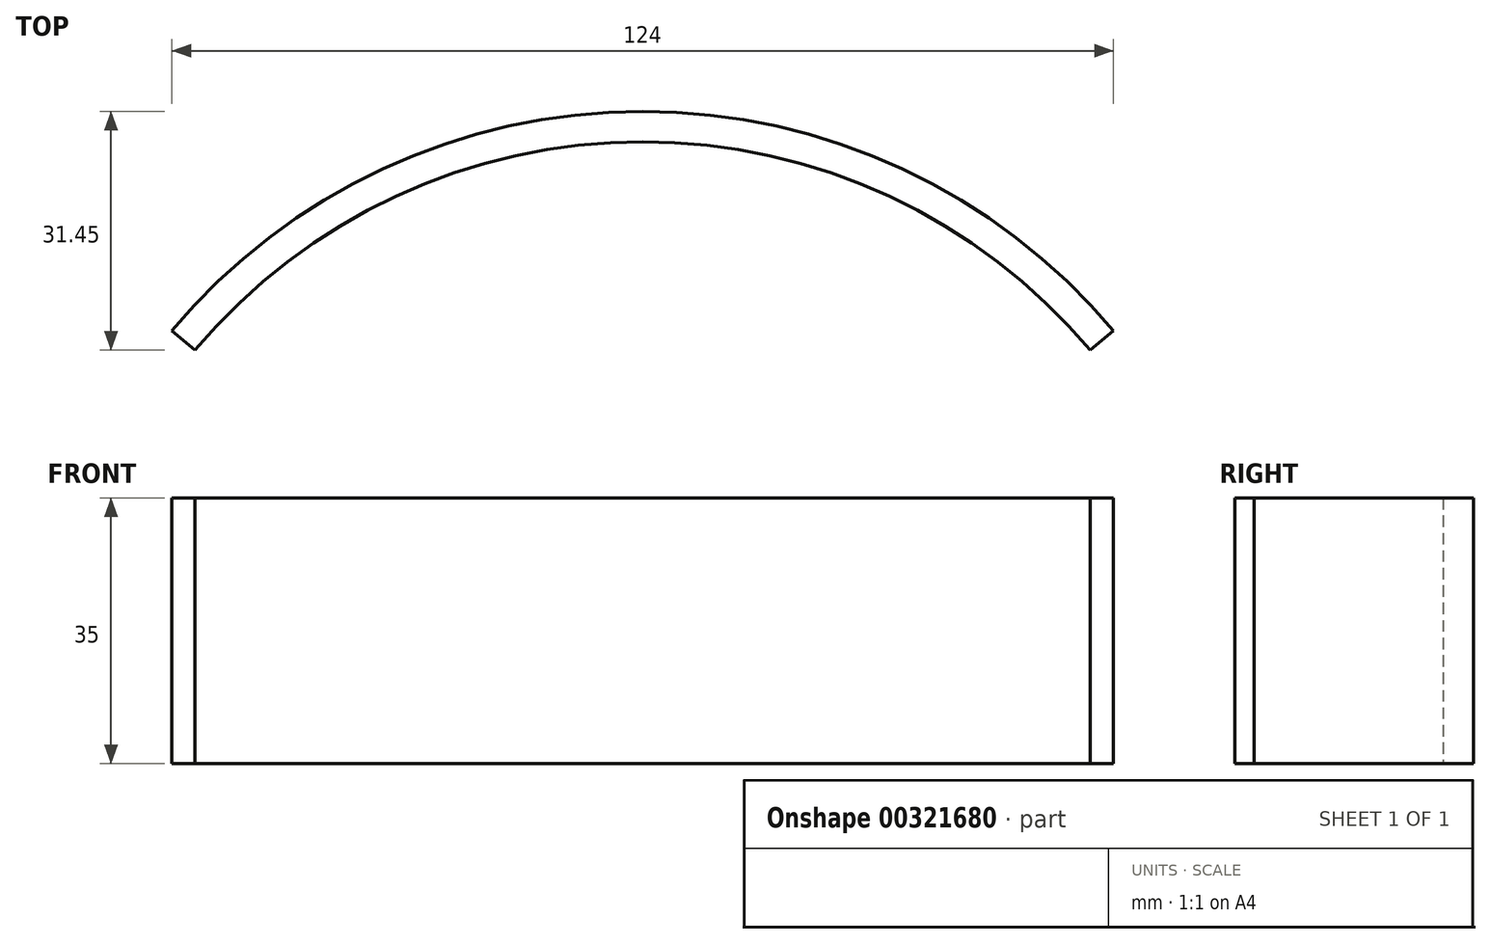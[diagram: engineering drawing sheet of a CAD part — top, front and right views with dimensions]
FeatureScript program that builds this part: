
annotation { "Feature Type Name" : "Feature", "Feature Type Description" : "" }
export const myFeature = defineFeature(function(context is Context, id is Id, definition is map)
    precondition{}
    {
        {
            var Q0;
            Q0=qCreatedBy(makeId("Top.planeOp"),FACE);
            var sketch = newSketch(context, id + "F0", { "sketchPlane" : qUnion([Q0])});
            skArc(sketch, "E0", {"start": v(62, 0) * mm, "mid": v(0, 28.88) * mm, "end": v(-62, 0) * mm});
            skArc(sketch, "E1.0", {"start": v(58.94, -2.57) * mm, "mid": v(0, 24.88) * mm, "end": v(-58.94, -2.57) * mm});
            skLineSegment(sketch, "E2", {"start": v(-62, 0) * mm, "end": v(-58.94, -2.57) * mm});
            skLineSegment(sketch, "E3", {"start": v(62, 0) * mm, "end": v(58.94, -2.57) * mm});
            skSolve(sketch);
        }
        {
            var Q0;
            Q0=makeQuery(id+"F0.imprint","IMPRINT",FACE,{"disambiguationData":[TD([[makeQuery(id+"F0.imprint","IMPRINT",EDGE,{"derivedFrom":sQuery(id+"F0.wireOp",EDGE,"E0")}),1.0]])]});
            extrude(context, id + "F1", {"entities" : qUnion([Q0]), "depth" : 35 * mm});
        }
    });
